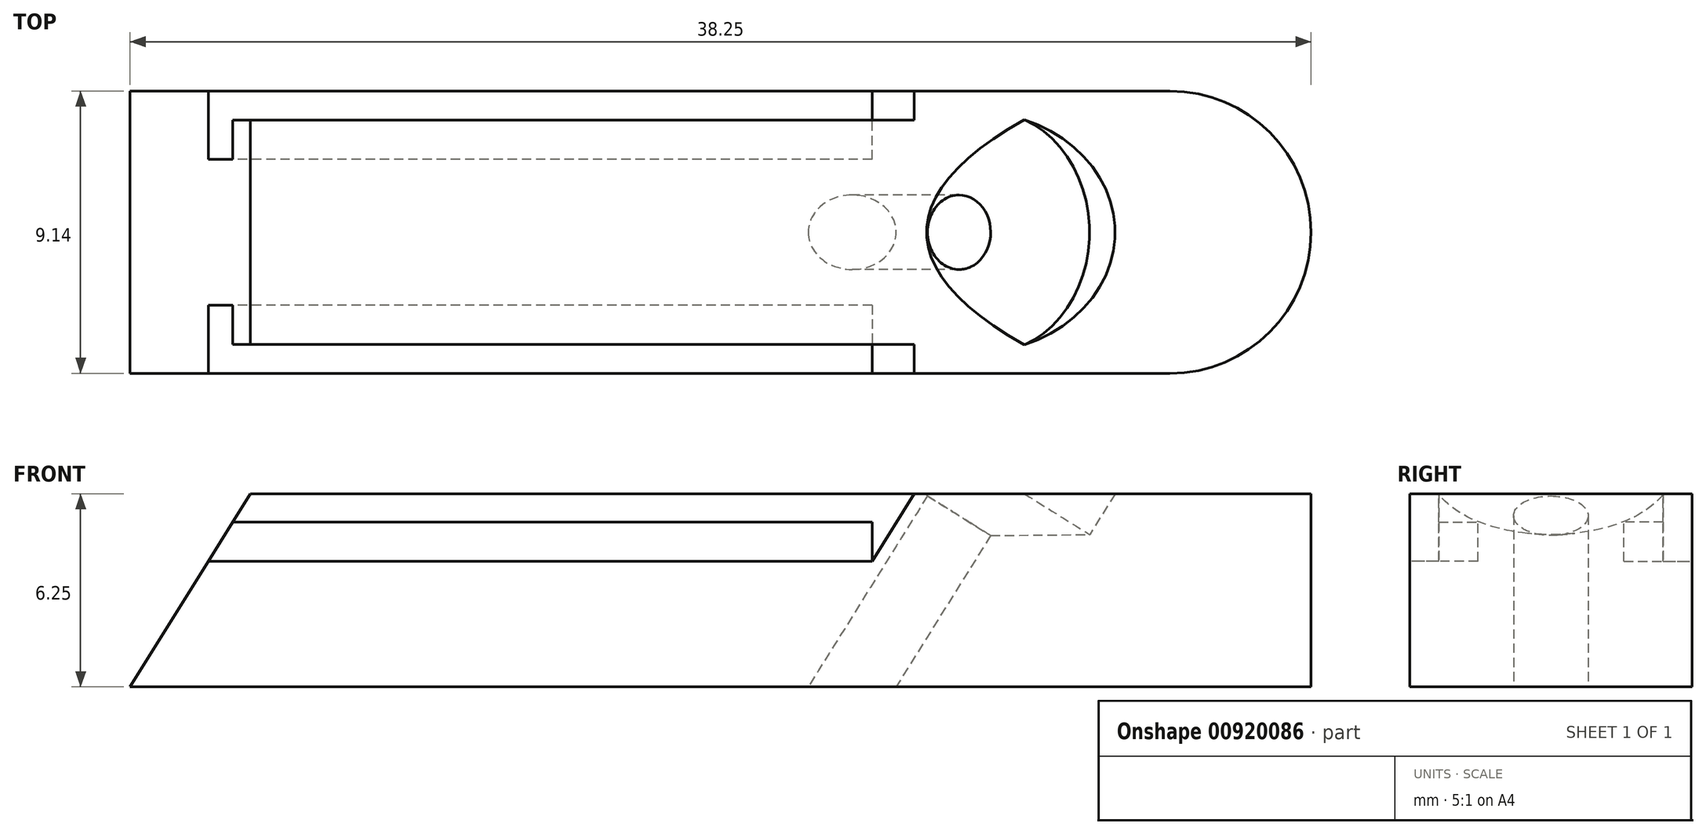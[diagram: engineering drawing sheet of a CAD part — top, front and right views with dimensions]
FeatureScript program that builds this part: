
annotation { "Feature Type Name" : "Feature", "Feature Type Description" : "" }
export const myFeature = defineFeature(function(context is Context, id is Id, definition is map)
    precondition{}
    {
        {
            var Q0;
            Q0=qCreatedBy(makeId("Top.planeOp"),FACE);
            var sketch = newSketch(context, id + "F0", { "sketchPlane" : qUnion([Q0])});
            skLineSegment(sketch, "E0", {"start": v(-23.4, 4.57) * mm, "end": v(-23.4, -4.57) * mm});
            skLineSegment(sketch, "E1", {"start": v(-23.4, -4.57) * mm, "end": v(10.29, -4.57) * mm});
            skLineSegment(sketch, "E2", {"start": v(10.29, 0) * mm, "end": v(10.29, 0) * mm});
            skLineSegment(sketch, "E3", {"start": v(10.29, 4.57) * mm, "end": v(-23.4, 4.57) * mm});
            skArc(sketch, "E4", {"start": v(10.29, -4.57) * mm, "mid": v(14.86, 0) * mm, "end": v(10.29, 4.57) * mm});
            skPoint(sketch, "E4.centerSnap0", {"position": v(10.29, 0) * mm});
            skSolve(sketch);
        }
        {
            var Q0;
            Q0 = qSketchRegion(id + "F0", true);
            extrude(context, id + "F1", {"entities" : qUnion([Q0]), "depth" : 6.25 * mm, "offsetDistance" : 25.4 * mm});
        }
        {
            var Q0;
            Q0=makeQuery(id+"F1.opExtrude","SWEPT_FACE",FACE,{"disambiguationData":[OSD([sQuery(id+"F0.wireOp",EDGE,"E3")])]});
            var sketch = newSketch(context, id + "F2", { "sketchPlane" : qUnion([Q0])});
            skLineSegment(sketch, "E5", {"start": v(-2, 6.25) * mm, "end": v(-0.64, 4.06) * mm});
            skLineSegment(sketch, "E6", {"start": v(-0.64, 4.06) * mm, "end": v(23.4, 4.06) * mm});
            skLineSegment(sketch, "E7", {"start": v(23.4, 4.06) * mm, "end": v(23.4, 6.25) * mm});
            skLineSegment(sketch, "E8", {"start": v(23.4, 6.25) * mm, "end": v(-2, 6.25) * mm});
            skSolve(sketch);
        }
        {
            var Q0;
            Q0=makeQuery(id+"F2.imprint","IMPRINT",FACE,{"disambiguationData":[TD([[makeQuery(id+"F2.imprint","IMPRINT",EDGE,{"derivedFrom":sQuery(id+"F2.wireOp",EDGE,"E5")}),1.0]])]});
            extrude(context, id + "F3", {"entities" : qUnion([Q0]), "operationType" : NewBodyOperationType.REMOVE, "oppositeDirection" : true, "depth" : 0.94 * mm, "offsetDistance" : 25.4 * mm});
        }
        {
            var Q0;
            Q0=makeQuery(id+"F3.boolean.opBoolean","COPY",FACE,{"derivedFrom":makeQuery(id+"F3.opExtrude","CAP_FACE",FACE,{"disambiguationData":[OSD([sQuery(id+"F2.wireOp",EDGE,"E5"),sQuery(id+"F2.wireOp",EDGE,"E6"),sQuery(id+"F2.wireOp",EDGE,"E7"),sQuery(id+"F2.wireOp",EDGE,"E8")])],"isStart":false})});
            var sketch = newSketch(context, id + "F4", { "sketchPlane" : qUnion([Q0])});
            skLineSegment(sketch, "E9.bottom", {"start": v(23.4, 4.06) * mm, "end": v(-0.64, 4.06) * mm});
            skLineSegment(sketch, "E9.top", {"start": v(23.4, 5.33) * mm, "end": v(-0.64, 5.33) * mm});
            skLineSegment(sketch, "E9.left", {"start": v(23.4, 4.06) * mm, "end": v(23.4, 5.33) * mm});
            skLineSegment(sketch, "E9.right", {"start": v(-0.64, 4.06) * mm, "end": v(-0.64, 5.33) * mm});
            skSolve(sketch);
        }
        {
            var Q0;
            Q0=makeQuery(id+"F4.imprint","IMPRINT",FACE,{"disambiguationData":[TD([[makeQuery(id+"F4.imprint","IMPRINT",EDGE,{"derivedFrom":sQuery(id+"F4.wireOp",EDGE,"E9.bottom")}),1.0]])]});
            extrude(context, id + "F5", {"entities" : qUnion([Q0]), "operationType" : NewBodyOperationType.REMOVE, "oppositeDirection" : true, "depth" : 1.27 * mm, "offsetDistance" : 25.4 * mm});
        }
        {
            var Q0;
            Q0=makeQuery(id+"F1.opExtrude","SWEPT_FACE",FACE,{"disambiguationData":[OSD([sQuery(id+"F0.wireOp",EDGE,"E3")])]});
            var sketch = newSketch(context, id + "F6", { "sketchPlane" : qUnion([Q0])});
            skLineSegment(sketch, "E10", {"start": v(23.4, 0) * mm, "end": v(19.49, 6.25) * mm});
            skLineSegment(sketch, "E11", {"start": v(19.49, 6.25) * mm, "end": v(23.4, 6.25) * mm});
            skLineSegment(sketch, "E12", {"start": v(23.4, 6.25) * mm, "end": v(23.4, 0) * mm});
            skSolve(sketch);
        }
        {
            var Q0;
            Q0 = qSketchRegion(id + "F6", true);
            extrude(context, id + "F7", {"entities" : qUnion([Q0]), "operationType" : NewBodyOperationType.REMOVE, "endBound" : BoundingType.THROUGH_ALL, "oppositeDirection" : true, "depth" : 25.4 * mm, "offsetDistance" : 25.4 * mm});
        }
        {
            var Q0;
            Q0=makeQuery(id+"F1.opExtrude","SWEPT_BODY",BODY,{"disambiguationData":[OSD([sQuery(id+"F0.wireOp",EDGE,"E0"),sQuery(id+"F0.wireOp",EDGE,"E1"),sQuery(id+"F0.wireOp",EDGE,"E3"),sQuery(id+"F0.wireOp",EDGE,"E4")])]});
            var Q1;
            Q1=qCreatedBy(makeId("Front.planeOp"),FACE);
            mirror(context, id + "F8", {"operationType" : NewBodyOperationType.INTERSECT, "entities" : qUnion([Q0]), "mirrorPlane" : qUnion([Q1])});
        }
        {
            var Q0;
            Q0=qCreatedBy(makeId("Front.planeOp"),FACE);
            var sketch = newSketch(context, id + "F9", { "sketchPlane" : qUnion([Q0])});
            skLineSegment(sketch, "E13", {"start": v(0, 0) * mm, "end": v(5.72, 9.15) * mm});
            skLineSegment(sketch, "E14", {"start": v(0, 0) * mm, "end": v(-1.35, -2.15) * mm});
            skLineSegment(sketch, "E15", {"start": v(-1.35, -2.15) * mm, "end": v(-0.32, -2.8) * mm});
            skLineSegment(sketch, "E16", {"start": v(-0.32, -2.8) * mm, "end": v(4.48, 4.9) * mm});
            skLineSegment(sketch, "E17", {"start": v(4.48, 4.9) * mm, "end": v(7.7, 4.93) * mm});
            skLineSegment(sketch, "E18", {"start": v(7.7, 4.93) * mm, "end": v(9.04, 7.08) * mm});
            skLineSegment(sketch, "E19", {"start": v(9.04, 7.08) * mm, "end": v(5.72, 9.15) * mm});
            skLineSegment(sketch, "E20", {"start": v(3.46, 5.54) * mm, "end": v(4.48, 4.9) * mm});
            skPoint(sketch, "E21.orphan", {"position": v(-2.37, -1.51) * mm});
            skPoint(sketch, "E22.orphan", {"position": v(2.4, 11.23) * mm});
            skSolve(sketch);
        }
        {
            var Q0;
            Q0 = qSketchRegion(id + "F9", true);
            var Q1;
            Q1=sQuery(id+"F9.wireOp",EDGE,"E13");
            revolve(context, id + "F10", {"operationType" : NewBodyOperationType.REMOVE, "surfaceOperationType" : NewSurfaceOperationType.NEW, "entities" : qUnion([Q0]), "axis" : qUnion([Q1]), "revolveType" : RevolveType.FULL});
        }
    });
